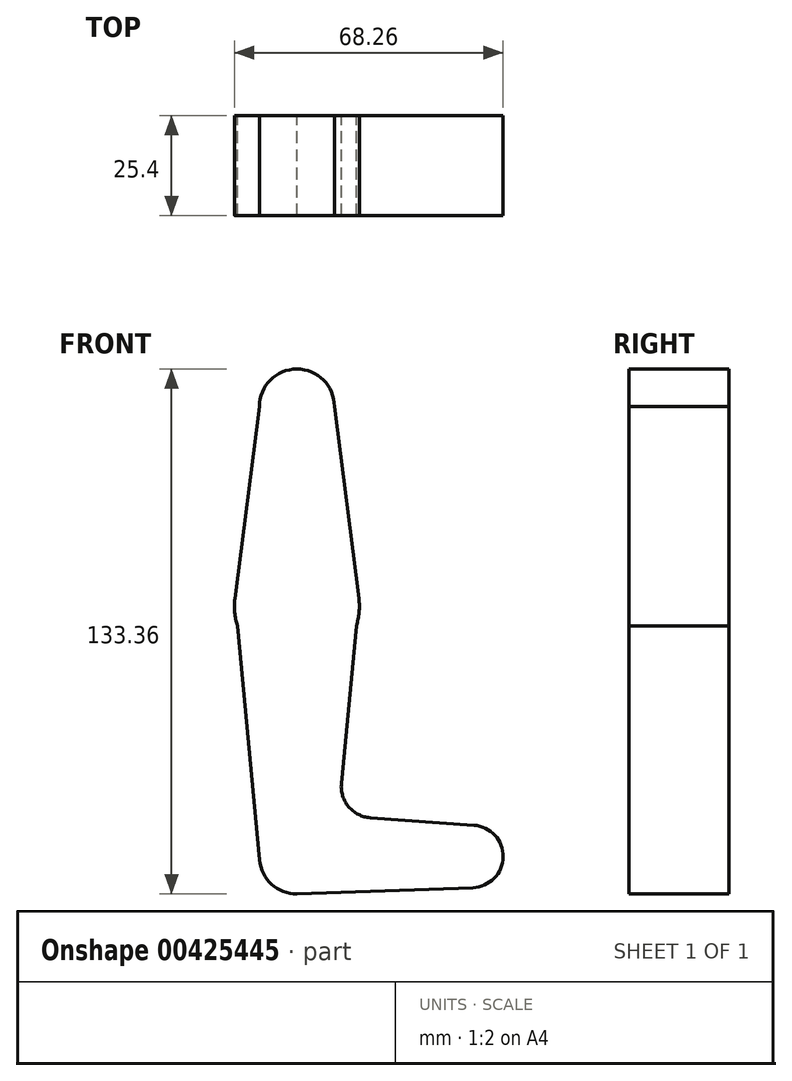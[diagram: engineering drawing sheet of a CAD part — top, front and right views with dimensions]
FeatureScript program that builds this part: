
annotation { "Feature Type Name" : "Feature", "Feature Type Description" : "" }
export const myFeature = defineFeature(function(context is Context, id is Id, definition is map)
    precondition{}
    {
        {
            var Q0;
            Q0=qCreatedBy(makeId("Front.planeOp"),FACE);
            var sketch = newSketch(context, id + "F0", { "sketchPlane" : qUnion([Q0])});
            skLineSegment(sketch, "E0", {"start": v(0, 0) * mm, "end": v(0, 114.3) * mm});
            skLineSegment(sketch, "E1", {"start": v(0, 0) * mm, "end": v(44.45, 0) * mm});
            skCircle(sketch, "E2", {"center": v(0, 0) * mm, "radius": 9.53 * mm});
            skCircle(sketch, "E3", {"center": v(0, 114.3) * mm, "radius": 9.53 * mm});
            skCircle(sketch, "E4", {"center": v(0, 63.5) * mm, "radius": 15.88 * mm});
            skCircle(sketch, "E5", {"center": v(44.45, 0) * mm, "radius": 7.94 * mm});
            skLineSegment(sketch, "E6", {"start": v(-9.52, 114.3) * mm, "end": v(-15.75, 65.5) * mm});
            skLineSegment(sketch, "E7", {"start": v(-15.75, 65.5) * mm, "end": v(-9.48, -0.9) * mm});
            skLineSegment(sketch, "E8", {"start": v(9.52, 114.3) * mm, "end": v(15.75, 65.5) * mm});
            skLineSegment(sketch, "E9", {"start": v(15.75, 65.5) * mm, "end": v(11.31, 18.5) * mm});
            skLineSegment(sketch, "E10", {"start": v(18.65, 9.82) * mm, "end": v(45.02, 7.92) * mm});
            skLineSegment(sketch, "E11", {"start": v(0, -9.52) * mm, "end": v(44.73, -7.93) * mm});
            skArc(sketch, "E12.filletArc", {"start": v(11.31, 18.5) * mm, "mid": v(13.16, 12.62) * mm, "end": v(18.65, 9.82) * mm});
            skPoint(sketch, "E13.orphan", {"position": v(-9.57, 0) * mm});
            skSolve(sketch);
        }
        {
            var Q0;
            {var subQ0=sQuery(id+"F0.wireOp",EDGE,"E7");var subQ1=sQuery(id+"F0.wireOp",EDGE,"E4");var subQ3=makeQuery(id+"F0.imprint","INTERSECT",VERTEX,{"derivedFrom":[subQ1,subQ0]});Q0=makeQuery(id+"F0.imprint","IMPRINT",FACE,{"disambiguationData":[TD([[makeQuery(id+"F0.imprint","IMPRINT",EDGE,{"disambiguationData":[TD([[subQ3,1.0]])],"derivedFrom":subQ1}),1.0]])]});}
            var Q1;
            {var subQ0=sQuery(id+"F0.wireOp",EDGE,"E9");var subQ1=sQuery(id+"F0.wireOp",EDGE,"E4");var subQ3=makeQuery(id+"F0.imprint","INTERSECT",VERTEX,{"derivedFrom":[subQ1,subQ0]});Q1=makeQuery(id+"F0.imprint","IMPRINT",FACE,{"disambiguationData":[TD([[makeQuery(id+"F0.imprint","IMPRINT",EDGE,{"disambiguationData":[TD([[subQ3,-1.0]])],"derivedFrom":subQ1}),1.0]])]});}
            var Q2;
            {var subQ0=sQuery(id+"F0.wireOp",EDGE,"E1");var subQ1=sQuery(id+"F0.wireOp",EDGE,"E0");var subQ2=makeQuery(id+"F0.imprint","INTERSECT",VERTEX,{"derivedFrom":[subQ1,subQ0]});Q2=makeQuery(id+"F0.imprint","IMPRINT",FACE,{"disambiguationData":[TD([[makeQuery(id+"F0.imprint","IMPRINT",EDGE,{"disambiguationData":[TD([[subQ2,-1.0]])],"derivedFrom":subQ1}),-1.0]])]});}
            var Q3;
            {var subQ0=sQuery(id+"F0.wireOp",EDGE,"E3");var subQ1=makeQuery(id+"F0.imprint","INTERSECT",VERTEX,{"derivedFrom":[subQ0,sQuery(id+"F0.wireOp",EDGE,"E6")]});Q3=makeQuery(id+"F0.imprint","IMPRINT",FACE,{"disambiguationData":[TD([[makeQuery(id+"F0.imprint","IMPRINT",EDGE,{"disambiguationData":[TD([[subQ1,1.0]])],"derivedFrom":subQ0}),1.0]])]});}
            var Q4;
            {var subQ0=sQuery(id+"F0.wireOp",EDGE,"E5");var subQ1=makeQuery(id+"F0.imprint","INTERSECT",VERTEX,{"derivedFrom":[subQ0,sQuery(id+"F0.wireOp",EDGE,"E10")]});Q4=makeQuery(id+"F0.imprint","IMPRINT",FACE,{"disambiguationData":[TD([[makeQuery(id+"F0.imprint","IMPRINT",EDGE,{"disambiguationData":[TD([[subQ1,-1.0]])],"derivedFrom":subQ0}),1.0]])]});}
            var Q5;
            {var subQ3=sQuery(id+"F0.wireOp",EDGE,"E0");var subQ6=sQuery(id+"F0.wireOp",EDGE,"E1");var subQ8=makeQuery(id+"F0.imprint","INTERSECT",VERTEX,{"derivedFrom":[subQ3,subQ6]});Q5=makeQuery(id+"F0.imprint","IMPRINT",FACE,{"disambiguationData":[TD([[makeQuery(id+"F0.imprint","IMPRINT",EDGE,{"disambiguationData":[TD([[subQ8,-1.0]])],"derivedFrom":subQ3}),1.0]])]});}
            var Q6;
            {var subQ0=sQuery(id+"F0.wireOp",EDGE,"E4");var subQ1=sQuery(id+"F0.wireOp",EDGE,"E0");var subQ2=makeQuery(id+"F0.imprint","INTERSECT",VERTEX,{"disambiguationData":[OD(0.0)],"derivedFrom":[subQ1,subQ0]});Q6=makeQuery(id+"F0.imprint","IMPRINT",FACE,{"disambiguationData":[TD([[makeQuery(id+"F0.imprint","IMPRINT",EDGE,{"disambiguationData":[TD([[subQ2,-1.0]])],"derivedFrom":subQ1}),1.0]])]});}
            var Q7;
            {var subQ5=sQuery(id+"F0.wireOp",EDGE,"E6");Q7=makeQuery(id+"F0.imprint","IMPRINT",FACE,{"disambiguationData":[TD([[makeQuery(id+"F0.imprint","IMPRINT",EDGE,{"derivedFrom":subQ5}),1.0]])]});}
            var Q8;
            {var subQ0=sQuery(id+"F0.wireOp",EDGE,"E5");var subQ1=sQuery(id+"F0.wireOp",EDGE,"E1");var subQ2=makeQuery(id+"F0.imprint","INTERSECT",VERTEX,{"derivedFrom":[subQ1,subQ0]});Q8=makeQuery(id+"F0.imprint","IMPRINT",FACE,{"disambiguationData":[TD([[makeQuery(id+"F0.imprint","IMPRINT",EDGE,{"disambiguationData":[TD([[subQ2,1.0]])],"derivedFrom":subQ1}),-1.0]])]});}
            var Q9;
            {var subQ0=sQuery(id+"F0.wireOp",EDGE,"E4");var subQ1=sQuery(id+"F0.wireOp",EDGE,"E0");var subQ2=makeQuery(id+"F0.imprint","INTERSECT",VERTEX,{"disambiguationData":[OD(0.0)],"derivedFrom":[subQ1,subQ0]});Q9=makeQuery(id+"F0.imprint","IMPRINT",FACE,{"disambiguationData":[TD([[makeQuery(id+"F0.imprint","IMPRINT",EDGE,{"disambiguationData":[TD([[subQ2,-1.0]])],"derivedFrom":subQ1}),-1.0]])]});}
            var Q10;
            {var subQ11=sQuery(id+"F0.wireOp",EDGE,"E10");Q10=makeQuery(id+"F0.imprint","IMPRINT",FACE,{"disambiguationData":[TD([[makeQuery(id+"F0.imprint","IMPRINT",EDGE,{"derivedFrom":subQ11}),-1.0]])]});}
            var Q11;
            {var subQ5=sQuery(id+"F0.wireOp",EDGE,"E8");Q11=makeQuery(id+"F0.imprint","IMPRINT",FACE,{"disambiguationData":[TD([[makeQuery(id+"F0.imprint","IMPRINT",EDGE,{"derivedFrom":subQ5}),-1.0]])]});}
            var Q12;
            {var subQ0=sQuery(id+"F0.wireOp",EDGE,"E2");var subQ1=sQuery(id+"F0.wireOp",EDGE,"E0");var subQ2=makeQuery(id+"F0.imprint","INTERSECT",VERTEX,{"derivedFrom":[subQ1,subQ0]});Q12=makeQuery(id+"F0.imprint","IMPRINT",FACE,{"disambiguationData":[TD([[makeQuery(id+"F0.imprint","IMPRINT",EDGE,{"disambiguationData":[TD([[subQ2,-1.0]])],"derivedFrom":subQ1}),1.0]])]});}
            extrude(context, id + "F1", {"entities" : qUnion([Q0, Q1, Q2, Q3, Q4, Q5, Q6, Q7, Q8, Q9, Q10, Q11, Q12]), "depth" : 25.4 * mm});
        }
    });
